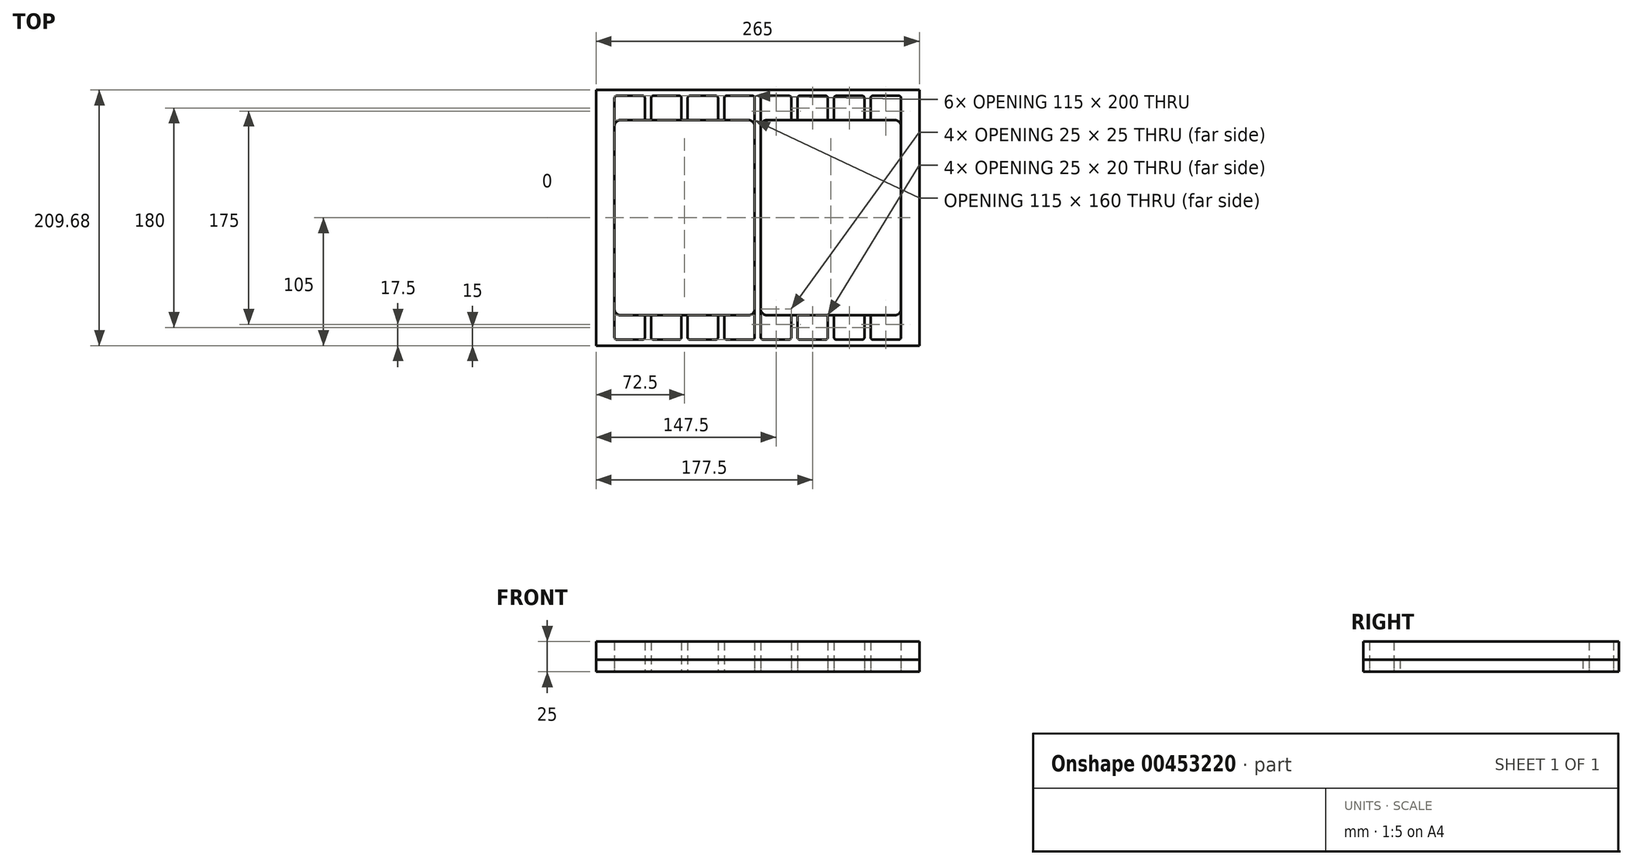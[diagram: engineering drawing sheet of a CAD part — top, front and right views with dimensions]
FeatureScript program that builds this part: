
annotation { "Feature Type Name" : "Feature", "Feature Type Description" : "" }
export const myFeature = defineFeature(function(context is Context, id is Id, definition is map)
    precondition{}
    {
        {
            var Q0;
            Q0=qCreatedBy(makeId("Top.planeOp"),FACE);
            var sketch = newSketch(context, id + "F0", { "sketchPlane" : qUnion([Q0])});
            skLineSegment(sketch, "E0.right", {"start": v(-132.5, 104.68) * mm, "end": v(-132.5, -105) * mm});
            skPoint(sketch, "E0.middle", {"position": v(0, 0) * mm});
            skLineSegment(sketch, "E1", {"start": v(-127.5, 95) * mm, "end": v(-127.5, -95) * mm});
            skLineSegment(sketch, "E2", {"start": v(0, 111.23) * mm, "end": v(0, -100) * mm, "construction": true});
            skLineSegment(sketch, "E3", {"start": v(-62.5, -80) * mm, "end": v(-62.5, -98) * mm});
            skLineSegment(sketch, "E4", {"start": v(-2.5, 75) * mm, "end": v(-2.5, -75) * mm});
            skLineSegment(sketch, "E5", {"start": v(-117.5, 75) * mm, "end": v(-117.5, -75) * mm});
            skLineSegment(sketch, "E6", {"start": v(-85.5, 100) * mm, "end": v(-64.5, 100) * mm});
            skLineSegment(sketch, "E7", {"start": v(-112.5, 80) * mm, "end": v(-7.5, 80) * mm});
            skLineSegment(sketch, "E8", {"start": v(-112.5, -80) * mm, "end": v(-7.5, -80) * mm});
            skArc(sketch, "E9.filletArc", {"start": v(-112.5, 80) * mm, "mid": v(-116.04, 78.54) * mm, "end": v(-117.5, 75) * mm});
            skArc(sketch, "E10.filletArc", {"start": v(-117.5, -75) * mm, "mid": v(-116.04, -78.54) * mm, "end": v(-112.5, -80) * mm});
            skPoint(sketch, "E11.newPointB", {"position": v(-2.5, -72.8) * mm});
            skArc(sketch, "E11.filletArc", {"start": v(-7.5, -80) * mm, "mid": v(-3.96, -78.54) * mm, "end": v(-2.5, -75) * mm});
            skPoint(sketch, "E12.newPointB", {"position": v(-2.5, 137.2) * mm});
            skArc(sketch, "E12.filletArc", {"start": v(-2.5, 75) * mm, "mid": v(-3.96, 78.54) * mm, "end": v(-7.5, 80) * mm});
            skLineSegment(sketch, "E13.trimOffspring", {"start": v(-92.5, -80) * mm, "end": v(-92.5, -98) * mm});
            skLineSegment(sketch, "E14.trimOffspring", {"start": v(-87.5, -80) * mm, "end": v(-87.5, -98) * mm});
            skLineSegment(sketch, "E15.trimOffspring", {"start": v(-57.5, -80) * mm, "end": v(-57.5, -98) * mm});
            skLineSegment(sketch, "E16.trimOffspring", {"start": v(-32.5, -80) * mm, "end": v(-32.5, -98) * mm});
            skLineSegment(sketch, "E17.trimOffspring", {"start": v(-27.5, -80) * mm, "end": v(-27.5, -98) * mm});
            skLineSegment(sketch, "E18", {"start": v(-117.5, 100) * mm, "end": v(-122.5, 100) * mm});
            skLineSegment(sketch, "E19", {"start": v(-117.5, -100) * mm, "end": v(-122.5, -100) * mm});
            skLineSegment(sketch, "E20", {"start": v(-2.5, 75) * mm, "end": v(-2.5, 98) * mm});
            skLineSegment(sketch, "E21", {"start": v(-117.5, 75) * mm, "end": v(-117.5, 98) * mm});
            skLineSegment(sketch, "E22", {"start": v(-117.5, -75) * mm, "end": v(-117.5, -98) * mm});
            skLineSegment(sketch, "E23", {"start": v(-92.5, 98) * mm, "end": v(-92.5, 80) * mm});
            skLineSegment(sketch, "E24", {"start": v(-87.5, 98) * mm, "end": v(-87.5, 80) * mm});
            skLineSegment(sketch, "E25", {"start": v(-62.5, 98) * mm, "end": v(-62.5, 80) * mm});
            skLineSegment(sketch, "E26", {"start": v(-57.5, 98) * mm, "end": v(-57.5, 80) * mm});
            skLineSegment(sketch, "E27", {"start": v(-32.5, 98) * mm, "end": v(-32.5, 80) * mm});
            skLineSegment(sketch, "E28", {"start": v(-27.5, 98) * mm, "end": v(-27.5, 80) * mm});
            skPoint(sketch, "E29.visualSharp", {"position": v(-117.5, 100) * mm});
            skArc(sketch, "E29.filletArc", {"start": v(-115.5, 100) * mm, "mid": v(-116.91, 99.41) * mm, "end": v(-117.5, 98) * mm});
            skArc(sketch, "E30.filletArc", {"start": v(-127.5, -95) * mm, "mid": v(-126.04, -98.54) * mm, "end": v(-122.5, -100) * mm});
            skArc(sketch, "E31.filletArc", {"start": v(-122.5, 100) * mm, "mid": v(-126.04, 98.54) * mm, "end": v(-127.5, 95) * mm});
            skArc(sketch, "E32.filletArc", {"start": v(-85.5, 100) * mm, "mid": v(-86.91, 99.41) * mm, "end": v(-87.5, 98) * mm});
            skArc(sketch, "E33.filletArc", {"start": v(-62.5, 98) * mm, "mid": v(-63.09, 99.41) * mm, "end": v(-64.5, 100) * mm});
            skLineSegment(sketch, "E34", {"start": v(-115.5, 100) * mm, "end": v(-94.5, 100) * mm});
            skLineSegment(sketch, "E35", {"start": v(-55.5, 100) * mm, "end": v(-34.5, 100) * mm});
            skLineSegment(sketch, "E36", {"start": v(-25.5, 100) * mm, "end": v(-4.5, 100) * mm});
            skPoint(sketch, "E37.visualSharp", {"position": v(-57.5, 100) * mm});
            skArc(sketch, "E37.filletArc", {"start": v(-55.5, 100) * mm, "mid": v(-56.91, 99.41) * mm, "end": v(-57.5, 98) * mm});
            skPoint(sketch, "E38.visualSharp", {"position": v(-32.5, 100) * mm});
            skArc(sketch, "E38.filletArc", {"start": v(-32.5, 98) * mm, "mid": v(-33.09, 99.41) * mm, "end": v(-34.5, 100) * mm});
            skPoint(sketch, "E39.visualSharp", {"position": v(-27.5, 100) * mm});
            skArc(sketch, "E39.filletArc", {"start": v(-25.5, 100) * mm, "mid": v(-26.91, 99.41) * mm, "end": v(-27.5, 98) * mm});
            skPoint(sketch, "E40.visualSharp", {"position": v(-2.5, 100) * mm});
            skArc(sketch, "E40.filletArc", {"start": v(-2.5, 98) * mm, "mid": v(-3.09, 99.41) * mm, "end": v(-4.5, 100) * mm});
            skPoint(sketch, "E41.visualSharp", {"position": v(-92.5, 100) * mm});
            skArc(sketch, "E41.filletArc", {"start": v(-92.5, 98) * mm, "mid": v(-93.09, 99.41) * mm, "end": v(-94.5, 100) * mm});
            skLineSegment(sketch, "E42", {"start": v(-115.5, -100) * mm, "end": v(-94.5, -100) * mm});
            skLineSegment(sketch, "E43", {"start": v(-85.5, -100) * mm, "end": v(-64.5, -100) * mm});
            skLineSegment(sketch, "E44", {"start": v(-55.5, -100) * mm, "end": v(-34.5, -100) * mm});
            skPoint(sketch, "E45.end.orphan", {"position": v(-2.5, -98.74) * mm});
            skLineSegment(sketch, "E46", {"start": v(-25.5, -100) * mm, "end": v(-4.5, -100) * mm});
            skPoint(sketch, "E47.end.orphan", {"position": v(-27.5, -90) * mm});
            skPoint(sketch, "E47.start.orphan", {"position": v(-1.25, -86.87) * mm});
            skLineSegment(sketch, "E48", {"start": v(-2.5, -75) * mm, "end": v(-2.5, -98) * mm});
            skPoint(sketch, "E49.visualSharp", {"position": v(-117.5, -100) * mm});
            skArc(sketch, "E49.filletArc", {"start": v(-117.5, -98) * mm, "mid": v(-116.91, -99.41) * mm, "end": v(-115.5, -100) * mm});
            skPoint(sketch, "E50.visualSharp", {"position": v(-92.5, -100) * mm});
            skArc(sketch, "E50.filletArc", {"start": v(-94.5, -100) * mm, "mid": v(-93.09, -99.41) * mm, "end": v(-92.5, -98) * mm});
            skPoint(sketch, "E51.visualSharp", {"position": v(-87.5, -100) * mm});
            skArc(sketch, "E51.filletArc", {"start": v(-87.5, -98) * mm, "mid": v(-86.91, -99.41) * mm, "end": v(-85.5, -100) * mm});
            skPoint(sketch, "E52.visualSharp", {"position": v(-57.5, -100) * mm});
            skArc(sketch, "E52.filletArc", {"start": v(-57.5, -98) * mm, "mid": v(-56.91, -99.41) * mm, "end": v(-55.5, -100) * mm});
            skPoint(sketch, "E53.visualSharp", {"position": v(-27.5, -100) * mm});
            skArc(sketch, "E53.filletArc", {"start": v(-27.5, -98) * mm, "mid": v(-26.91, -99.41) * mm, "end": v(-25.5, -100) * mm});
            skPoint(sketch, "E54.visualSharp", {"position": v(-62.5, -100) * mm});
            skArc(sketch, "E54.filletArc", {"start": v(-64.5, -100) * mm, "mid": v(-63.09, -99.41) * mm, "end": v(-62.5, -98) * mm});
            skPoint(sketch, "E55.visualSharp", {"position": v(-32.5, -100) * mm});
            skArc(sketch, "E55.filletArc", {"start": v(-34.5, -100) * mm, "mid": v(-33.09, -99.41) * mm, "end": v(-32.5, -98) * mm});
            skLineSegment(sketch, "E56.trimOffspring", {"start": v(0, -105) * mm, "end": v(0, -113.3) * mm, "construction": true});
            skPoint(sketch, "E57.visualSharp", {"position": v(-2.5, -100) * mm});
            skArc(sketch, "E57.filletArc", {"start": v(-4.5, -100) * mm, "mid": v(-3.09, -99.41) * mm, "end": v(-2.5, -98) * mm});
            skLineSegment(sketch, "E58", {"start": v(-132.5, -105) * mm, "end": v(0, -105) * mm});
            skLineSegment(sketch, "E59", {"start": v(-132.5, 104.68) * mm, "end": v(0, 104.68) * mm});
            skLineSegment(sketch, "E60.MirrorCS", {"start": v(117.5, 100) * mm, "end": v(122.5, 100) * mm});
            skArc(sketch, "E61.MirrorCS", {"start": v(92.5, 98) * mm, "mid": v(93.09, 99.41) * mm, "end": v(94.5, 100) * mm});
            skArc(sketch, "E62.MirrorCS", {"start": v(25.5, 100) * mm, "mid": v(26.91, 99.41) * mm, "end": v(27.5, 98) * mm});
            skArc(sketch, "E63.MirrorCS", {"start": v(7.5, -80) * mm, "mid": v(3.96, -78.54) * mm, "end": v(2.5, -75) * mm});
            skArc(sketch, "E64.MirrorCS", {"start": v(57.5, -98) * mm, "mid": v(56.91, -99.41) * mm, "end": v(55.5, -100) * mm});
            skArc(sketch, "E65.MirrorCS", {"start": v(115.5, 100) * mm, "mid": v(116.91, 99.41) * mm, "end": v(117.5, 98) * mm});
            skArc(sketch, "E66.MirrorCS", {"start": v(34.5, -100) * mm, "mid": v(33.09, -99.41) * mm, "end": v(32.5, -98) * mm});
            skArc(sketch, "E67.MirrorCS", {"start": v(55.5, 100) * mm, "mid": v(56.91, 99.41) * mm, "end": v(57.5, 98) * mm});
            skArc(sketch, "E68.MirrorCS", {"start": v(94.5, -100) * mm, "mid": v(93.09, -99.41) * mm, "end": v(92.5, -98) * mm});
            skArc(sketch, "E69.MirrorCS", {"start": v(32.5, 98) * mm, "mid": v(33.09, 99.41) * mm, "end": v(34.5, 100) * mm});
            skArc(sketch, "E70.MirrorCS", {"start": v(27.5, -98) * mm, "mid": v(26.91, -99.41) * mm, "end": v(25.5, -100) * mm});
            skArc(sketch, "E71.MirrorCS", {"start": v(64.5, -100) * mm, "mid": v(63.09, -99.41) * mm, "end": v(62.5, -98) * mm});
            skArc(sketch, "E72.MirrorCS", {"start": v(117.5, -98) * mm, "mid": v(116.91, -99.41) * mm, "end": v(115.5, -100) * mm});
            skArc(sketch, "E73.MirrorCS", {"start": v(2.5, 75) * mm, "mid": v(3.96, 78.54) * mm, "end": v(7.5, 80) * mm});
            skArc(sketch, "E74.MirrorCS", {"start": v(4.5, -100) * mm, "mid": v(3.09, -99.41) * mm, "end": v(2.5, -98) * mm});
            skArc(sketch, "E75.MirrorCS", {"start": v(2.5, 98) * mm, "mid": v(3.09, 99.41) * mm, "end": v(4.5, 100) * mm});
            skArc(sketch, "E76.MirrorCS", {"start": v(87.5, -98) * mm, "mid": v(86.91, -99.41) * mm, "end": v(85.5, -100) * mm});
            skLineSegment(sketch, "E77.MirrorCS", {"start": v(117.5, -100) * mm, "end": v(122.5, -100) * mm});
            skArc(sketch, "E78.MirrorCS", {"start": v(127.5, -95) * mm, "mid": v(126.04, -98.54) * mm, "end": v(122.5, -100) * mm});
            skArc(sketch, "E79.MirrorCS", {"start": v(112.5, 80) * mm, "mid": v(116.04, 78.54) * mm, "end": v(117.5, 75) * mm});
            skArc(sketch, "E80.MirrorCS", {"start": v(117.5, -75) * mm, "mid": v(116.04, -78.54) * mm, "end": v(112.5, -80) * mm});
            skArc(sketch, "E81.MirrorCS", {"start": v(85.5, 100) * mm, "mid": v(86.91, 99.41) * mm, "end": v(87.5, 98) * mm});
            skArc(sketch, "E82.MirrorCS", {"start": v(62.5, 98) * mm, "mid": v(63.09, 99.41) * mm, "end": v(64.5, 100) * mm});
            skLineSegment(sketch, "E83.MirrorCS", {"start": v(32.5, 98) * mm, "end": v(32.5, 80) * mm});
            skLineSegment(sketch, "E84.MirrorCS", {"start": v(2.5, 75) * mm, "end": v(2.5, 98) * mm});
            skArc(sketch, "E85.MirrorCS", {"start": v(122.5, 100) * mm, "mid": v(126.04, 98.54) * mm, "end": v(127.5, 95) * mm});
            skLineSegment(sketch, "E86.MirrorCS", {"start": v(27.5, 98) * mm, "end": v(27.5, 80) * mm});
            skLineSegment(sketch, "E87.MirrorCS", {"start": v(117.5, -75) * mm, "end": v(117.5, -98) * mm});
            skLineSegment(sketch, "E88.MirrorCS", {"start": v(117.5, 75) * mm, "end": v(117.5, 98) * mm});
            skLineSegment(sketch, "E89.MirrorCS", {"start": v(92.5, 98) * mm, "end": v(92.5, 80) * mm});
            skLineSegment(sketch, "E90.MirrorCS", {"start": v(62.5, 98) * mm, "end": v(62.5, 80) * mm});
            skLineSegment(sketch, "E91.MirrorCS", {"start": v(115.5, 100) * mm, "end": v(94.5, 100) * mm});
            skLineSegment(sketch, "E92.MirrorCS", {"start": v(27.5, -80) * mm, "end": v(27.5, -98) * mm});
            skLineSegment(sketch, "E93.MirrorCS", {"start": v(57.5, 98) * mm, "end": v(57.5, 80) * mm});
            skLineSegment(sketch, "E94.MirrorCS", {"start": v(87.5, 98) * mm, "end": v(87.5, 80) * mm});
            skLineSegment(sketch, "E95.MirrorCS", {"start": v(32.5, -80) * mm, "end": v(32.5, -98) * mm});
            skLineSegment(sketch, "E96.MirrorCS", {"start": v(2.5, -75) * mm, "end": v(2.5, -98) * mm});
            skLineSegment(sketch, "E97.MirrorCS", {"start": v(132.5, 104.68) * mm, "end": v(0, 104.68) * mm});
            skLineSegment(sketch, "E98.MirrorCS", {"start": v(112.5, -80) * mm, "end": v(7.5, -80) * mm});
            skLineSegment(sketch, "E99.MirrorCS", {"start": v(87.5, -80) * mm, "end": v(87.5, -98) * mm});
            skLineSegment(sketch, "E100.MirrorCS", {"start": v(25.5, -100) * mm, "end": v(4.5, -100) * mm});
            skPoint(sketch, "E101.MirrorP", {"position": v(32.5, 100) * mm});
            skLineSegment(sketch, "E102.MirrorCS", {"start": v(127.5, 95) * mm, "end": v(127.5, -95) * mm});
            skLineSegment(sketch, "E103.MirrorCS", {"start": v(2.5, 75) * mm, "end": v(2.5, -75) * mm});
            skLineSegment(sketch, "E104.MirrorCS", {"start": v(132.5, 104.68) * mm, "end": v(132.5, -105) * mm});
            skPoint(sketch, "E105.MirrorP", {"position": v(27.5, -100) * mm});
            skPoint(sketch, "E106.MirrorP", {"position": v(92.5, -100) * mm});
            skLineSegment(sketch, "E107.MirrorCS", {"start": v(25.5, 100) * mm, "end": v(4.5, 100) * mm});
            skPoint(sketch, "E108.MirrorP", {"position": v(32.5, -100) * mm});
            skLineSegment(sketch, "E109.MirrorCS", {"start": v(62.5, -80) * mm, "end": v(62.5, -98) * mm});
            skPoint(sketch, "E110.MirrorP", {"position": v(117.5, 100) * mm});
            skLineSegment(sketch, "E111.MirrorCS", {"start": v(92.5, -80) * mm, "end": v(92.5, -98) * mm});
            skLineSegment(sketch, "E112.MirrorCS", {"start": v(85.5, 100) * mm, "end": v(64.5, 100) * mm});
            skLineSegment(sketch, "E113.MirrorCS", {"start": v(57.5, -80) * mm, "end": v(57.5, -98) * mm});
            skLineSegment(sketch, "E114.MirrorCS", {"start": v(117.5, 75) * mm, "end": v(117.5, -75) * mm});
            skPoint(sketch, "E115.MirrorP", {"position": v(57.5, -100) * mm});
            skPoint(sketch, "E116.MirrorP", {"position": v(2.5, -100) * mm});
            skLineSegment(sketch, "E117.MirrorCS", {"start": v(132.5, -105) * mm, "end": v(0, -105) * mm});
            skLineSegment(sketch, "E118.MirrorCS", {"start": v(55.5, -100) * mm, "end": v(34.5, -100) * mm});
            skPoint(sketch, "E119.MirrorP", {"position": v(1.25, -86.87) * mm});
            skPoint(sketch, "E120.MirrorP", {"position": v(27.5, 100) * mm});
            skPoint(sketch, "E121.MirrorP", {"position": v(27.5, -90) * mm});
            skLineSegment(sketch, "E122.MirrorCS", {"start": v(112.5, 80) * mm, "end": v(7.5, 80) * mm});
            skPoint(sketch, "E123.MirrorP", {"position": v(2.5, 100) * mm});
            skPoint(sketch, "E124.MirrorP", {"position": v(57.5, 100) * mm});
            skPoint(sketch, "E125.MirrorP", {"position": v(117.5, -100) * mm});
            skPoint(sketch, "E126.MirrorP", {"position": v(62.5, -100) * mm});
            skPoint(sketch, "E127.MirrorP", {"position": v(92.5, 100) * mm});
            skPoint(sketch, "E128.MirrorP", {"position": v(2.5, -72.8) * mm});
            skPoint(sketch, "E129.MirrorP", {"position": v(87.5, -100) * mm});
            skLineSegment(sketch, "E130.MirrorCS", {"start": v(55.5, 100) * mm, "end": v(34.5, 100) * mm});
            skPoint(sketch, "E131.MirrorP", {"position": v(2.5, -98.74) * mm});
            skLineSegment(sketch, "E132.MirrorCS", {"start": v(85.5, -100) * mm, "end": v(64.5, -100) * mm});
            skLineSegment(sketch, "E133.MirrorCS", {"start": v(115.5, -100) * mm, "end": v(94.5, -100) * mm});
            skSolve(sketch);
        }
        {
            var Q0;
            Q0=qCreatedBy(makeId("Front.planeOp"),FACE);
            var sketch = newSketch(context, id + "F1", { "sketchPlane" : qUnion([Q0])});
            skSolve(sketch);
        }
        {
            var Q0;
            Q0=qCreatedBy(makeId("Top.planeOp"),FACE);
            var sketch = newSketch(context, id + "F2", { "sketchPlane" : qUnion([Q0])});
            skSolve(sketch);
        }
        {
            var Q0;
            {var subQ1=sQuery(id+"F0.wireOp",EDGE,"0b8ad8bd-77e3-4ca3-a08b-48bf14f2aca2.trimOffspring");Q0=makeQuery(id+"F0.imprint","IMPRINT",FACE,{"disambiguationData":[TD([[makeQuery(id+"F0.imprint","IMPRINT",EDGE,{"derivedFrom":subQ1}),-1.0]])]});}
            var Q1;
            Q1=makeQuery(id+"F0.imprint","IMPRINT",FACE,{"disambiguationData":[TD([[makeQuery(id+"F0.imprint","IMPRINT",EDGE,{"derivedFrom":sQuery(id+"F0.wireOp",EDGE,"E6")}),-1.0]])]});
            var Q2;
            {var subQ1=sQuery(id+"F0.wireOp",EDGE,"E26");Q2=makeQuery(id+"F0.imprint","IMPRINT",FACE,{"disambiguationData":[TD([[makeQuery(id+"F0.imprint","IMPRINT",EDGE,{"derivedFrom":subQ1}),1.0]])]});}
            var Q3;
            {var subQ1=sQuery(id+"F0.wireOp",EDGE,"E12.filletArc");Q3=makeQuery(id+"F0.imprint","IMPRINT",FACE,{"disambiguationData":[TD([[makeQuery(id+"F0.imprint","IMPRINT",EDGE,{"derivedFrom":subQ1}),-1.0]])]});}
            var Q4;
            {var subQ2=sQuery(id+"F0.wireOp",EDGE,"fWcC9iDX-iXsm-b3cJ-IEPL-r1TJ8NqgpBr9");Q4=makeQuery(id+"F0.imprint","IMPRINT",FACE,{"disambiguationData":[TD([[makeQuery(id+"F0.imprint","IMPRINT",EDGE,{"derivedFrom":subQ2}),-1.0]])]});}
            var Q5;
            {var subQ1=sQuery(id+"F0.wireOp",EDGE,"0RSXPC5l-d7ya-xAhc-zCtb-8mzQv6jsdDoj");Q5=makeQuery(id+"F0.imprint","IMPRINT",FACE,{"disambiguationData":[TD([[makeQuery(id+"F0.imprint","IMPRINT",EDGE,{"derivedFrom":subQ1}),-1.0]])]});}
            var Q6;
            {var subQ1=sQuery(id+"F0.wireOp",EDGE,"pxOEOSkn-Ruv8-1Q8q-YSbH-tcCFeD32e2Dk");Q6=makeQuery(id+"F0.imprint","IMPRINT",FACE,{"disambiguationData":[TD([[makeQuery(id+"F0.imprint","IMPRINT",EDGE,{"derivedFrom":subQ1}),-1.0]])]});}
            var Q7;
            {var subQ2=sQuery(id+"F0.wireOp",EDGE,"XXeh42Ws-biLA-BUaU-cjRT-GfOQdVRKKhKH");Q7=makeQuery(id+"F0.imprint","IMPRINT",FACE,{"disambiguationData":[TD([[makeQuery(id+"F0.imprint","IMPRINT",EDGE,{"derivedFrom":subQ2}),1.0]])]});}
            var Q8;
            {var subQ0=sQuery(id+"F0.wireOp",EDGE,"E10.filletArc");Q8=makeQuery(id+"F0.imprint","IMPRINT",FACE,{"disambiguationData":[TD([[makeQuery(id+"F0.imprint","IMPRINT",EDGE,{"derivedFrom":subQ0}),-1.0]])]});}
            var Q9;
            {var subQ0=sQuery(id+"F0.wireOp",EDGE,"E3");Q9=makeQuery(id+"F0.imprint","IMPRINT",FACE,{"disambiguationData":[TD([[makeQuery(id+"F0.imprint","IMPRINT",EDGE,{"derivedFrom":subQ0}),-1.0]])]});}
            var Q10;
            {var subQ0=sQuery(id+"F0.wireOp",EDGE,"E15.trimOffspring");Q10=makeQuery(id+"F0.imprint","IMPRINT",FACE,{"disambiguationData":[TD([[makeQuery(id+"F0.imprint","IMPRINT",EDGE,{"derivedFrom":subQ0}),1.0]])]});}
            var Q11;
            {var subQ3=sQuery(id+"F0.wireOp",EDGE,"E11.filletArc");Q11=makeQuery(id+"F0.imprint","IMPRINT",FACE,{"disambiguationData":[TD([[makeQuery(id+"F0.imprint","IMPRINT",EDGE,{"derivedFrom":subQ3}),-1.0]])]});}
            var Q12;
            {var subQ0=sQuery(id+"F0.wireOp",EDGE,"efec4cbf-bafa-4433-a108-ff534f5d5ed3.trimOffspring");Q12=makeQuery(id+"F0.imprint","IMPRINT",FACE,{"disambiguationData":[TD([[makeQuery(id+"F0.imprint","IMPRINT",EDGE,{"derivedFrom":subQ0}),1.0]])]});}
            var Q13;
            {var subQ0=sQuery(id+"F0.wireOp",EDGE,"79d70a1f-d73e-4382-9638-068996a91a96.trimOffspring");Q13=makeQuery(id+"F0.imprint","IMPRINT",FACE,{"disambiguationData":[TD([[makeQuery(id+"F0.imprint","IMPRINT",EDGE,{"derivedFrom":subQ0}),1.0]])]});}
            var Q14;
            Q14=makeQuery(id+"F0.imprint","IMPRINT",FACE,{"disambiguationData":[TD([[makeQuery(id+"F0.imprint","IMPRINT",EDGE,{"derivedFrom":sQuery(id+"F0.wireOp",EDGE,"0OWyduE2-Y3gO-b06X-Ja89-CY0GqTVAfCY9")}),1.0]])]});
            var Q15;
            {var subQ1=sQuery(id+"F0.wireOp",EDGE,"E0.right");Q15=makeQuery(id+"F0.imprint","IMPRINT",FACE,{"disambiguationData":[TD([[makeQuery(id+"F0.imprint","IMPRINT",EDGE,{"derivedFrom":subQ1}),1.0]])]});}
            var Q16;
            {var subQ0=sQuery(id+"F0.wireOp",EDGE,"E0.left");Q16=makeQuery(id+"F0.imprint","IMPRINT",FACE,{"disambiguationData":[TD([[makeQuery(id+"F0.imprint","IMPRINT",EDGE,{"derivedFrom":subQ0}),-1.0]])]});}
            var Q17;
            {var subQ1=sQuery(id+"F0.wireOp",EDGE,"E9.filletArc");Q17=makeQuery(id+"F0.imprint","IMPRINT",FACE,{"disambiguationData":[TD([[makeQuery(id+"F0.imprint","IMPRINT",EDGE,{"derivedFrom":subQ1}),-1.0]])]});}
            var Q18;
            Q18=qSketchRegion(id+"F1",true);
            extrude(context, id + "F3", {"entities" : qUnion([Q0, Q1, Q2, Q3, Q4, Q5, Q6, Q7, Q8, Q9, Q10, Q11, Q12, Q13, Q14, Q15, Q16, Q17, Q18]), "depth" : 10 * mm});
        }
        {
            var Q0;
            Q0=makeQuery(id+"F0.imprint","IMPRINT",FACE,{"disambiguationData":[TD([[makeQuery(id+"F0.imprint","IMPRINT",EDGE,{"derivedFrom":sQuery(id+"F0.wireOp",EDGE,"E62.MirrorCS")}),-1.0]])]});
            var Q1;
            Q1=makeQuery(id+"F0.imprint","IMPRINT",FACE,{"disambiguationData":[TD([[makeQuery(id+"F0.imprint","IMPRINT",EDGE,{"derivedFrom":sQuery(id+"F0.wireOp",EDGE,"E67.MirrorCS")}),-1.0]])]});
            var Q2;
            Q2=makeQuery(id+"F0.imprint","IMPRINT",FACE,{"disambiguationData":[TD([[makeQuery(id+"F0.imprint","IMPRINT",EDGE,{"derivedFrom":sQuery(id+"F0.wireOp",EDGE,"E81.MirrorCS")}),-1.0]])]});
            var Q3;
            Q3=makeQuery(id+"F0.imprint","IMPRINT",FACE,{"disambiguationData":[TD([[makeQuery(id+"F0.imprint","IMPRINT",EDGE,{"derivedFrom":sQuery(id+"F0.wireOp",EDGE,"E61.MirrorCS")}),-1.0]])]});
            var Q4;
            Q4=makeQuery(id+"F0.imprint","IMPRINT",FACE,{"disambiguationData":[TD([[makeQuery(id+"F0.imprint","IMPRINT",EDGE,{"derivedFrom":sQuery(id+"F0.wireOp",EDGE,"E68.MirrorCS")}),-1.0]])]});
            var Q5;
            Q5=makeQuery(id+"F0.imprint","IMPRINT",FACE,{"disambiguationData":[TD([[makeQuery(id+"F0.imprint","IMPRINT",EDGE,{"derivedFrom":sQuery(id+"F0.wireOp",EDGE,"E71.MirrorCS")}),-1.0]])]});
            var Q6;
            Q6=makeQuery(id+"F0.imprint","IMPRINT",FACE,{"disambiguationData":[TD([[makeQuery(id+"F0.imprint","IMPRINT",EDGE,{"derivedFrom":sQuery(id+"F0.wireOp",EDGE,"E64.MirrorCS")}),-1.0]])]});
            var Q7;
            {var subQ1=sQuery(id+"F0.wireOp",EDGE,"E63.MirrorCS");Q7=makeQuery(id+"F0.imprint","IMPRINT",FACE,{"disambiguationData":[TD([[makeQuery(id+"F0.imprint","IMPRINT",EDGE,{"derivedFrom":subQ1}),1.0]])]});}
            extrude(context, id + "F4", {"entities" : qUnion([Q0, Q1, Q2, Q3, Q4, Q5, Q6, Q7]), "operationType" : NewBodyOperationType.ADD, "depth" : 10 * mm});
        }
        {
            var Q0;
            Q0=qCreatedBy(makeId("Top.planeOp"),FACE);
            var sketch = newSketch(context, id + "F5", { "sketchPlane" : qUnion([Q0])});
            skSolve(sketch);
        }
        {
            var Q0;
            Q0=qSketchRegion(id+"F0",true);
            extrude(context, id + "F6", {"entities" : qUnion([Q0]), "depth" : 25 * mm});
        }
        {
            var Q0;
            Q0=qSketchRegion(id+"F5",true);
            var Q1;
            Q1=qSketchRegion(id+"F0",true);
            var Q2;
            Q2=qSketchRegion(id+"F2",true);
            extrude(context, id + "F7", {"entities" : qUnion([Q0, Q1, Q2]), "depth" : 25 * mm});
        }
        {
            var Q0;
            Q0=qSketchRegion(id+"F0",true);
            extrude(context, id + "F8", {"entities" : qUnion([Q0]), "depth" : 25 * mm});
        }
    });
